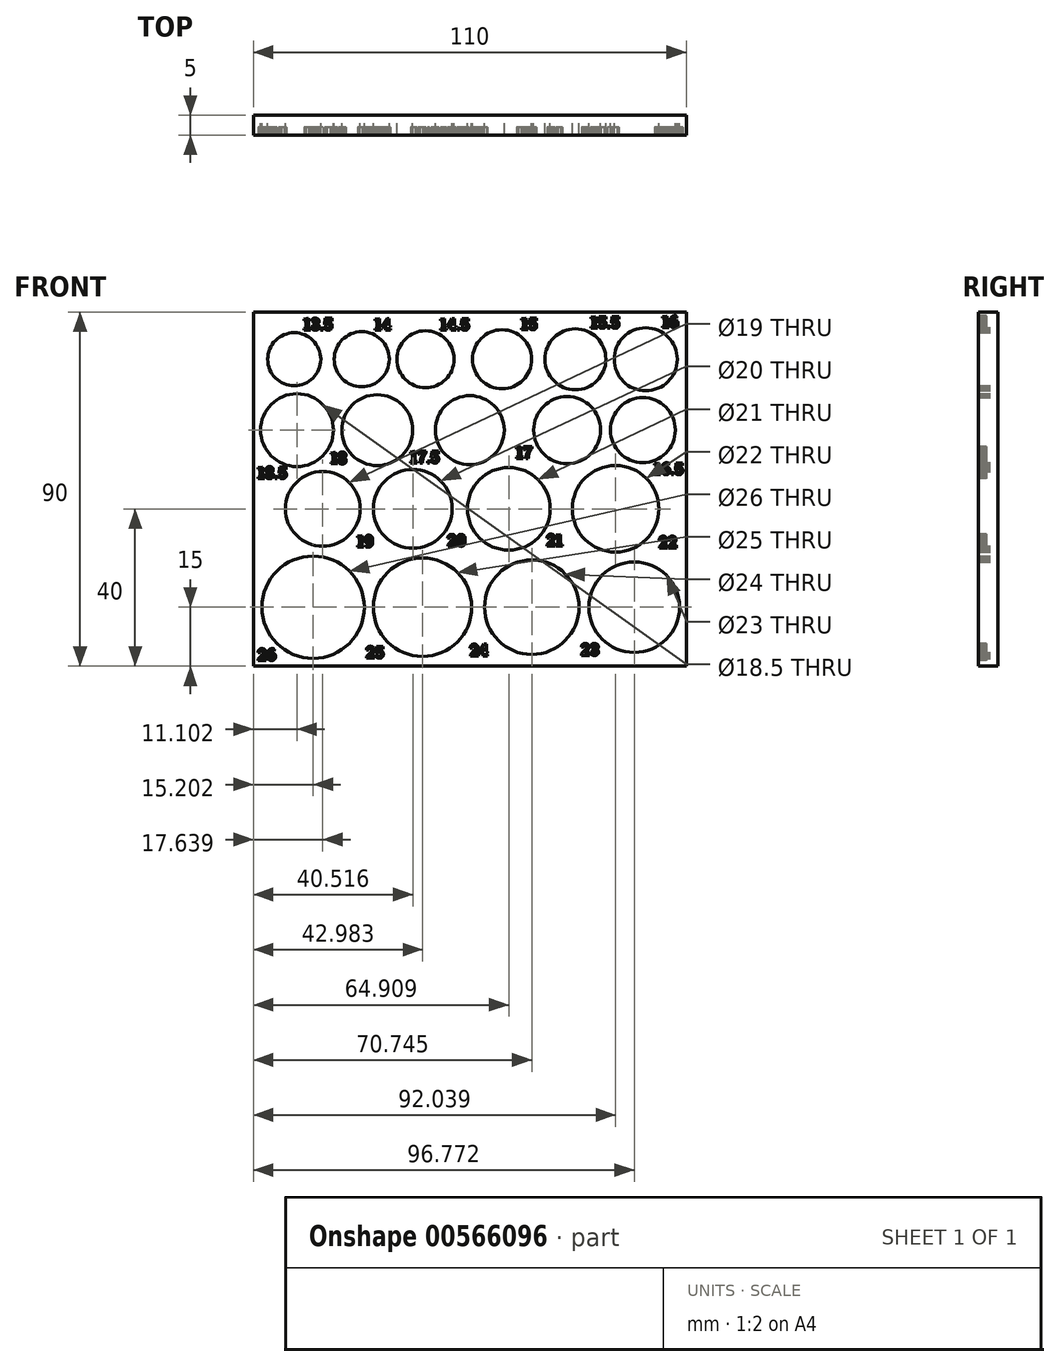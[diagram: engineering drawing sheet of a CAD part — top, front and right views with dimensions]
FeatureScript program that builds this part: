
annotation { "Feature Type Name" : "Feature", "Feature Type Description" : "" }
export const myFeature = defineFeature(function(context is Context, id is Id, definition is map)
    precondition{}
    {
        {
            var Q0;
            Q0=qCreatedBy(makeId("Front.planeOp"),FACE);
            var sketch = newSketch(context, id + "F0", { "sketchPlane" : qUnion([Q0])});
            skLineSegment(sketch, "E0.bottom", {"start": v(55, -45) * mm, "end": v(-55, -45) * mm});
            skLineSegment(sketch, "E0.top", {"start": v(55, 45) * mm, "end": v(-55, 45) * mm});
            skLineSegment(sketch, "E0.left", {"start": v(55, -45) * mm, "end": v(55, 45) * mm});
            skLineSegment(sketch, "E0.right", {"start": v(-55, -45) * mm, "end": v(-55, 45) * mm});
            skPoint(sketch, "E0.middle", {"position": v(0, 0) * mm});
            skLineSegment(sketch, "E1", {"start": v(-55, -45) * mm, "end": v(-55, -5) * mm});
            skLineSegment(sketch, "E2", {"start": v(-55, -5) * mm, "end": v(55, -5) * mm});
            skCircle(sketch, "E3", {"center": v(37.04, -5) * mm, "radius": 11 * mm});
            skCircle(sketch, "E4", {"center": v(9.9, -5) * mm, "radius": 10.5 * mm});
            skCircle(sketch, "E5", {"center": v(-14.48, -5) * mm, "radius": 10 * mm});
            skCircle(sketch, "E6", {"center": v(-37.36, -5) * mm, "radius": 9.5 * mm});
            skLineSegment(sketch, "E7", {"start": v(-55, -5) * mm, "end": v(-55, 15) * mm});
            skLineSegment(sketch, "E8", {"start": v(-55, 15) * mm, "end": v(55, 15) * mm});
            skCircle(sketch, "E9", {"center": v(0, 15) * mm, "radius": 8.75 * mm});
            skCircle(sketch, "E10", {"center": v(-23.52, 15) * mm, "radius": 9 * mm});
            skCircle(sketch, "E11", {"center": v(-43.9, 15) * mm, "radius": 9.25 * mm});
            skCircle(sketch, "E12", {"center": v(24.73, 15) * mm, "radius": 8.5 * mm});
            skCircle(sketch, "E13", {"center": v(43.96, 15) * mm, "radius": 8.25 * mm});
            skLineSegment(sketch, "E14", {"start": v(-55, 15) * mm, "end": v(-55, 33) * mm});
            skLineSegment(sketch, "E15", {"start": v(-55, 33) * mm, "end": v(55, 33) * mm});
            skCircle(sketch, "E16", {"center": v(44.7, 33) * mm, "radius": 8 * mm});
            skLineSegment(sketch, "E17", {"start": v(-55, -45) * mm, "end": v(-55, -30) * mm});
            skLineSegment(sketch, "E18", {"start": v(-55, -30) * mm, "end": v(55, -30) * mm});
            skCircle(sketch, "E19", {"center": v(41.77, -30) * mm, "radius": 11.5 * mm});
            skCircle(sketch, "E20", {"center": v(15.74, -30) * mm, "radius": 12 * mm});
            skCircle(sketch, "E21", {"center": v(-12.02, -30) * mm, "radius": 12.5 * mm});
            skCircle(sketch, "E22", {"center": v(-39.8, -30) * mm, "radius": 13 * mm});
            skCircle(sketch, "E23", {"center": v(26.82, 33) * mm, "radius": 7.75 * mm});
            skCircle(sketch, "E24", {"center": v(8.2, 33) * mm, "radius": 7.5 * mm});
            skCircle(sketch, "E25", {"center": v(-11.26, 33) * mm, "radius": 7.25 * mm});
            skCircle(sketch, "E26", {"center": v(-27.45, 33) * mm, "radius": 7 * mm});
            skCircle(sketch, "E27", {"center": v(-44.6, 33) * mm, "radius": 6.75 * mm});
            skSolve(sketch);
        }
        {
            var Q0;
            {var subQ9=sQuery(id+"F0.wireOp",EDGE,"E8");var subQ38=sQuery(id+"F0.wireOp",EDGE,"E0.left");var subQ39=makeQuery(id+"F0.imprint","INTERSECT",VERTEX,{"derivedFrom":[subQ38,subQ9]});var subQ55=sQuery(id+"F0.wireOp",EDGE,"E2");var subQ68=makeQuery(id+"F0.imprint","INTERSECT",VERTEX,{"derivedFrom":[subQ38,subQ55]});var subQ74=sQuery(id+"F0.wireOp",EDGE,"E18");var subQ84=makeQuery(id+"F0.imprint","INTERSECT",VERTEX,{"derivedFrom":[subQ38,subQ74]});var subQ94=sQuery(id+"F0.wireOp",EDGE,"E0.top");var subQ95=sQuery(id+"F0.wireOp",EDGE,"E0.bottom");Q0=qUnion([makeQuery(id+"F0.imprint","IMPRINT",FACE,{"disambiguationData":[TD([[makeQuery(id+"F0.imprint","IMPRINT",EDGE,{"derivedFrom":subQ95}),-1.0]])]}),makeQuery(id+"F0.imprint","IMPRINT",FACE,{"disambiguationData":[TD([[makeQuery(id+"F0.imprint","IMPRINT",EDGE,{"derivedFrom":subQ94}),1.0]])]}),makeQuery(id+"F0.imprint","IMPRINT",FACE,{"disambiguationData":[TD([[makeQuery(id+"F0.imprint","IMPRINT",EDGE,{"disambiguationData":[TD([[subQ84,-1.0]])],"derivedFrom":subQ38}),1.0]])]}),makeQuery(id+"F0.imprint","IMPRINT",FACE,{"disambiguationData":[TD([[makeQuery(id+"F0.imprint","IMPRINT",EDGE,{"disambiguationData":[TD([[subQ68,-1.0]])],"derivedFrom":subQ38}),1.0]])]}),makeQuery(id+"F0.imprint","IMPRINT",FACE,{"disambiguationData":[TD([[makeQuery(id+"F0.imprint","IMPRINT",EDGE,{"disambiguationData":[TD([[subQ39,-1.0]])],"derivedFrom":subQ38}),1.0]])]})]);}
            extrude(context, id + "F1", {"entities" : qUnion([Q0]), "depth" : 5 * mm, "offsetDistance" : 25 * mm});
        }
        {
            var Q0;
            Q0=makeQuery(id+"F1.opExtrude","CAP_FACE",FACE,{"disambiguationData":[OSD([sQuery(id+"F0.wireOp",EDGE,"E0.bottom"),sQuery(id+"F0.wireOp",EDGE,"E0.top"),sQuery(id+"F0.wireOp",EDGE,"E0.left"),sQuery(id+"F0.wireOp",EDGE,"E0.right"),sQuery(id+"F0.wireOp",EDGE,"E3"),sQuery(id+"F0.wireOp",EDGE,"E4"),sQuery(id+"F0.wireOp",EDGE,"E5"),sQuery(id+"F0.wireOp",EDGE,"E6"),sQuery(id+"F0.wireOp",EDGE,"E9"),sQuery(id+"F0.wireOp",EDGE,"E10"),sQuery(id+"F0.wireOp",EDGE,"E11"),sQuery(id+"F0.wireOp",EDGE,"E12"),sQuery(id+"F0.wireOp",EDGE,"E13"),sQuery(id+"F0.wireOp",EDGE,"E16"),sQuery(id+"F0.wireOp",EDGE,"E19"),sQuery(id+"F0.wireOp",EDGE,"E20"),sQuery(id+"F0.wireOp",EDGE,"E21"),sQuery(id+"F0.wireOp",EDGE,"E22"),sQuery(id+"F0.wireOp",EDGE,"E23"),sQuery(id+"F0.wireOp",EDGE,"E24"),sQuery(id+"F0.wireOp",EDGE,"E25"),sQuery(id+"F0.wireOp",EDGE,"E26"),sQuery(id+"F0.wireOp",EDGE,"E27")])],"isStart":false});
            var sketch = newSketch(context, id + "F2", { "sketchPlane" : qUnion([Q0])});
            skText(sketch, "E28", { "text": "26", "fontName": "RobotoSlab-Bold.ttf"});
            skText(sketch, "E29", { "text": "25", "fontName": "RobotoSlab-Bold.ttf"});
            skText(sketch, "E30", { "text": "24", "fontName": "RobotoSlab-Bold.ttf"});
            skText(sketch, "E31", { "text": "23", "fontName": "RobotoSlab-Bold.ttf"});
            skText(sketch, "E32", { "text": "21", "fontName": "RobotoSlab-Bold.ttf"});
            skText(sketch, "E33", { "text": "22", "fontName": "RobotoSlab-Bold.ttf"});
            skText(sketch, "E34", { "text": "20", "fontName": "RobotoSlab-Bold.ttf"});
            skText(sketch, "E35", { "text": "19", "fontName": "RobotoSlab-Bold.ttf"});
            skText(sketch, "E36", { "text": "18.5", "fontName": "RobotoSlab-Bold.ttf"});
            skText(sketch, "E37", { "text": "18", "fontName": "RobotoSlab-Bold.ttf"});
            skText(sketch, "E38", { "text": "17.5", "fontName": "RobotoSlab-Bold.ttf"});
            skText(sketch, "E39", { "text": "17", "fontName": "RobotoSlab-Bold.ttf"});
            skText(sketch, "E40", { "text": "16.5", "fontName": "RobotoSlab-Bold.ttf"});
            skText(sketch, "E41", { "text": "16", "fontName": "RobotoSlab-Bold.ttf"});
            skText(sketch, "E42", { "text": "15.5", "fontName": "RobotoSlab-Bold.ttf"});
            skText(sketch, "E43", { "text": "15", "fontName": "RobotoSlab-Bold.ttf"});
            skText(sketch, "E44", { "text": "14.5", "fontName": "RobotoSlab-Bold.ttf"});
            skText(sketch, "E45", { "text": "14", "fontName": "RobotoSlab-Bold.ttf"});
            skText(sketch, "E46", { "text": "13.5", "fontName": "RobotoSlab-Bold.ttf"});
            const initialGuessF2  = {"E28": [-0.0539, -0.04352, 1, 0, 0.003], "E29": [-0.02638, -0.04292, 1, 0, 0.003], "E30": [0, -0.04237, 1, 0, 0.003], "E31": [0.02823, -0.04221, 1, 0, 0.003], "E32": [0.0195, -0.01444, 1, 0, 0.003], "E33": [0.04801, -0.01494, 1, 0, 0.003], "E34": [-0.0057, -0.01448, 1, 0, 0.003], "E35": [-0.02867, -0.0147, 1, 0, 0.003], "E36": [-0.05387, 0.00271, 1, 0, 0.003], "E37": [-0.03539, 0.00644, 1, 0, 0.003], "E38": [-0.01515, 0.00667, 1, 0, 0.003], "E39": [0.01173, 0.00782, 1, 0, 0.003], "E40": [0.04677, 0.0037, 1, 0, 0.003], "E41": [0.04885, 0.04104, 1, 0, 0.003], "E42": [0.03068, 0.0409, 1, 0, 0.003], "E43": [0.01304, 0.04052, 1, 0, 0.003], "E44": [-0.00762, 0.0404, 1, 0, 0.003], "E45": [-0.02422, 0.04042, 1, 0, 0.003], "E46": [-0.04224, 0.04044, 1, 0, 0.003]};
            skSetInitialGuess(sketch, initialGuessF2);
            skSolve(sketch);
        }
        {
            var Q0;
            Q0 = qSketchRegion(id + "F2", true);
            extrude(context, id + "F3", {"entities" : qUnion([Q0]), "operationType" : NewBodyOperationType.REMOVE, "oppositeDirection" : true, "depth" : 2 * mm, "offsetDistance" : 25 * mm});
        }
    });
